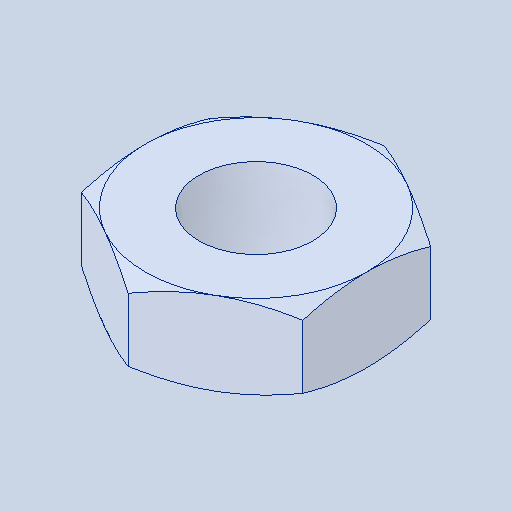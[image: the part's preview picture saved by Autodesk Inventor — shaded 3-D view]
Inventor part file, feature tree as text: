
AUTODESK INVENTOR PART (.ipt)
format: ipt  version: 2023.4 (Build 274418000, 418)  size: 116,224 bytes
history: native  units: in
note: dims shown in document units (in); Inventor stores cm internally (conversion verified against a paired STEP export)
features: mirror x1
ambient origin geometry x8: Origin, YZ Plane, XZ Plane, XY Plane, X Axis, Y Axis, Z Axis, Center Point
bodies: Solid1 (feature_tree)
feature tree (1):
  mirror  "Mirror1"
